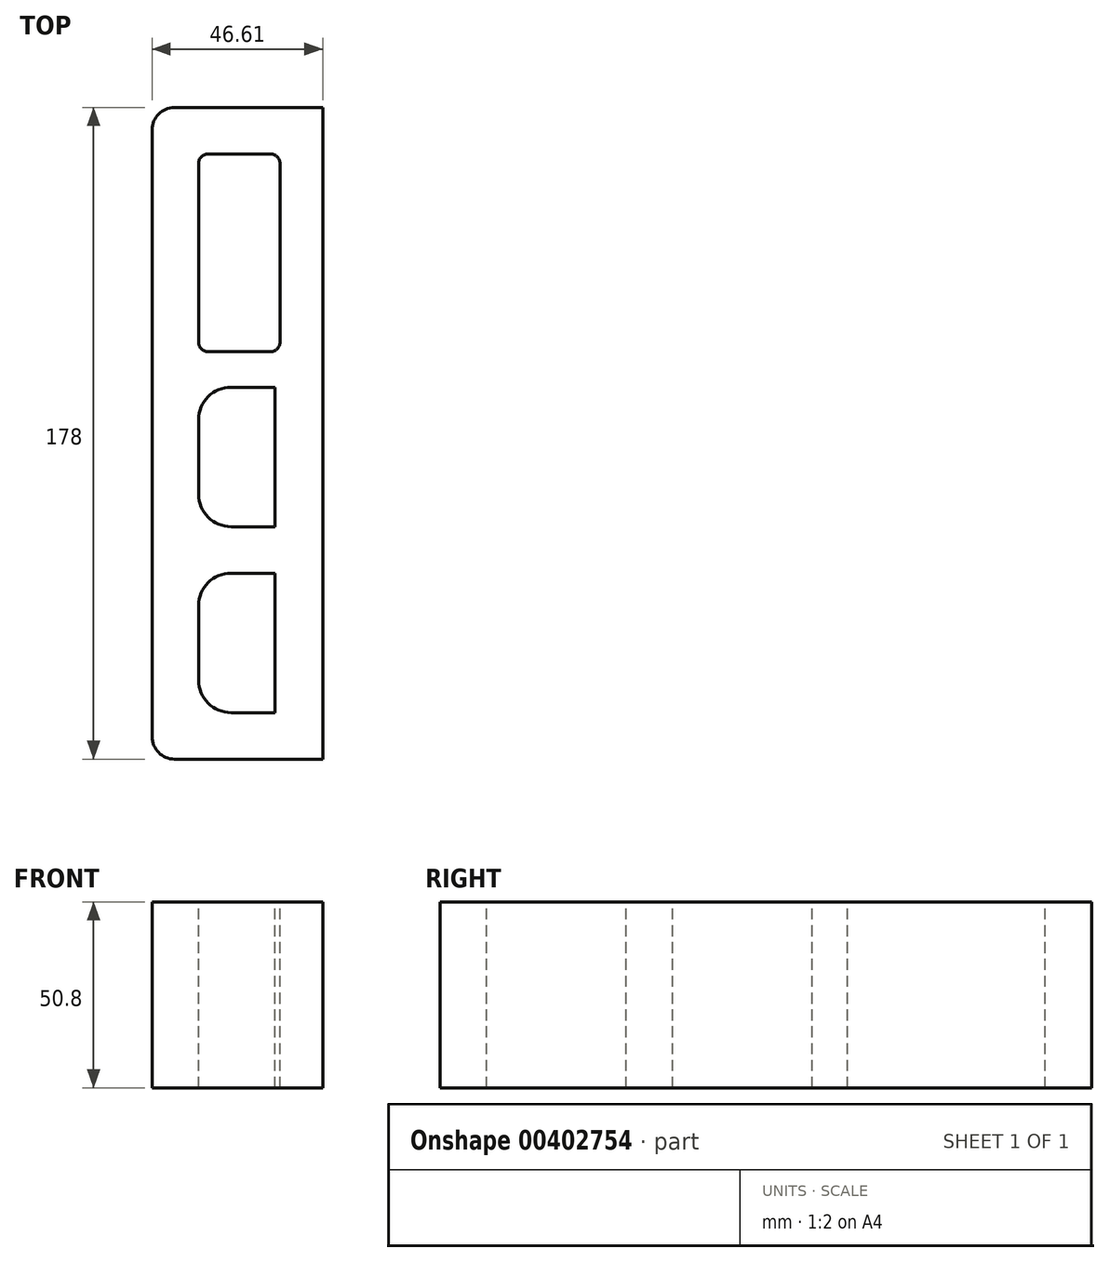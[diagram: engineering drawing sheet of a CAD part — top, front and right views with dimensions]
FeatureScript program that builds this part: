
annotation { "Feature Type Name" : "Feature", "Feature Type Description" : "" }
export const myFeature = defineFeature(function(context is Context, id is Id, definition is map)
    precondition{}
    {
        {
            var Q0;
            Q0=qCreatedBy(makeId("Top.planeOp"),FACE);
            var sketch = newSketch(context, id + "F0", { "sketchPlane" : qUnion([Q0])});
            skLineSegment(sketch, "E0", {"start": v(-117.43, 89) * mm, "end": v(117.43, -89) * mm, "construction": true});
            skLineSegment(sketch, "E1", {"start": v(117.43, 89) * mm, "end": v(0, 0) * mm, "construction": true});
            skArc(sketch, "E2", {"start": v(-70.48, 61.75) * mm, "mid": v(-79.05, 58.35) * mm, "end": v(-83.6, 50.33) * mm, "construction": true});
            skArc(sketch, "E3", {"start": v(-79.19, 70.45) * mm, "mid": v(-88.89, 80.1) * mm, "end": v(-98.64, 70.5) * mm, "construction": true});
            skArc(sketch, "E4", {"start": v(-98.68, -70.37) * mm, "mid": v(-88.97, -80.06) * mm, "end": v(-79.13, -70.5) * mm, "construction": true});
            skArc(sketch, "E5", {"start": v(-60.91, 9.68) * mm, "mid": v(-61.6, -0.56) * mm, "end": v(-60.92, -10.8) * mm});
            skLineSegment(sketch, "E6", {"start": v(-79.19, 70.45) * mm, "end": v(-70.48, 70.45) * mm, "construction": true});
            skLineSegment(sketch, "E7", {"start": v(-70.48, 70.45) * mm, "end": v(-70.48, 61.75) * mm, "construction": true});
            skLineSegment(sketch, "E8", {"start": v(-83.6, 50.33) * mm, "end": v(-83.6, 22.87) * mm, "construction": true});
            skLineSegment(sketch, "E9", {"start": v(-83.6, 22.87) * mm, "end": v(-77.26, 22.87) * mm, "construction": true});
            skLineSegment(sketch, "E10", {"start": v(-77.26, 22.87) * mm, "end": v(-77.26, -10.83) * mm, "construction": true});
            skLineSegment(sketch, "E11", {"start": v(-77.26, -10.83) * mm, "end": v(-70.83, -10.83) * mm, "construction": true});
            skLineSegment(sketch, "E12", {"start": v(-70.83, -10.83) * mm, "end": v(-70.83, -70.5) * mm, "construction": true});
            skLineSegment(sketch, "E13", {"start": v(-70.83, -70.5) * mm, "end": v(-79.13, -70.5) * mm, "construction": true});
            skLineSegment(sketch, "E14", {"start": v(-98.68, -70.37) * mm, "end": v(-105.43, -65.75) * mm, "construction": true});
            skLineSegment(sketch, "E15", {"start": v(-108.04, -64.7) * mm, "end": v(-108.04, -60.76) * mm, "construction": true});
            skLineSegment(sketch, "E16", {"start": v(-108.04, -60.76) * mm, "end": v(-106.9, -60.74) * mm, "construction": true});
            skLineSegment(sketch, "E17", {"start": v(-106.9, -60.74) * mm, "end": v(-106.9, 53.14) * mm, "construction": true});
            skLineSegment(sketch, "E18", {"start": v(-106.9, 53.14) * mm, "end": v(-108.07, 53.14) * mm, "construction": true});
            skLineSegment(sketch, "E19", {"start": v(-108.07, 53.14) * mm, "end": v(-108.07, 57.12) * mm, "construction": true});
            skLineSegment(sketch, "E20", {"start": v(-108.07, 57.12) * mm, "end": v(-106.9, 57.12) * mm, "construction": true});
            skLineSegment(sketch, "E21", {"start": v(-106.9, 57.12) * mm, "end": v(-107.04, 63.36) * mm, "construction": true});
            skLineSegment(sketch, "E22", {"start": v(-107.04, 63.36) * mm, "end": v(-98.64, 70.5) * mm, "construction": true});
            skArc(sketch, "E23", {"start": v(-9.49, 78.12) * mm, "mid": v(-18.8, 73.53) * mm, "end": v(-27.4, 67.74) * mm});
            skArc(sketch, "E24", {"start": v(75.52, 67.88) * mm, "mid": v(66.9, 73.6) * mm, "end": v(57.61, 78.19) * mm});
            skArc(sketch, "E25", {"start": v(108.1, -9.7) * mm, "mid": v(108.7, 0.59) * mm, "end": v(108.05, 10.87) * mm});
            skArc(sketch, "E26", {"start": v(56.9, -78.11) * mm, "mid": v(66.08, -73.32) * mm, "end": v(74.54, -67.34) * mm});
            skArc(sketch, "E27", {"start": v(-28.12, -67.82) * mm, "mid": v(-19.56, -73.56) * mm, "end": v(-10.29, -78.05) * mm});
            skArc(sketch, "E28", {"start": v(-28.4, 60.74) * mm, "mid": v(-45.75, 39.78) * mm, "end": v(-55.21, 14.26) * mm});
            skArc(sketch, "E29", {"start": v(50.94, 75.43) * mm, "mid": v(24.1, 80.05) * mm, "end": v(-2.74, 75.43) * mm});
            skArc(sketch, "E30", {"start": v(82.84, 54.94) * mm, "mid": v(79.78, 57.95) * mm, "end": v(76.52, 60.75) * mm});
            skArc(sketch, "E31", {"start": v(102.32, 15.8) * mm, "mid": v(101.51, 20.16) * mm, "end": v(100.4, 24.44) * mm});
            skArc(sketch, "E32", {"start": v(75.47, -60.27) * mm, "mid": v(92.86, -39.3) * mm, "end": v(102.35, -13.78) * mm});
            skArc(sketch, "E33", {"start": v(-3.58, -75.5) * mm, "mid": v(23.34, -80.12) * mm, "end": v(50.25, -75.43) * mm});
            skArc(sketch, "E34", {"start": v(-35.4, -54.87) * mm, "mid": v(-32.33, -57.87) * mm, "end": v(-29.07, -60.67) * mm});
            skArc(sketch, "E35", {"start": v(-55.22, -15.34) * mm, "mid": v(-54.43, -19.69) * mm, "end": v(-53.33, -23.97) * mm});
            skLineSegment(sketch, "E36", {"start": v(-55.22, -15.34) * mm, "end": v(-60.92, -10.8) * mm});
            skLineSegment(sketch, "E37", {"start": v(-60.91, 9.68) * mm, "end": v(-55.21, 14.26) * mm});
            skLineSegment(sketch, "E38", {"start": v(-28.4, 60.74) * mm, "end": v(-27.4, 67.74) * mm});
            skLineSegment(sketch, "E39", {"start": v(-9.49, 78.12) * mm, "end": v(-2.74, 75.43) * mm});
            skLineSegment(sketch, "E40", {"start": v(50.94, 75.43) * mm, "end": v(57.61, 78.19) * mm});
            skLineSegment(sketch, "E41", {"start": v(75.52, 67.88) * mm, "end": v(76.52, 60.75) * mm});
            skLineSegment(sketch, "E42", {"start": v(102.32, 15.8) * mm, "end": v(108.05, 10.87) * mm});
            skLineSegment(sketch, "E43", {"start": v(108.1, -9.7) * mm, "end": v(102.35, -13.78) * mm});
            skLineSegment(sketch, "E44", {"start": v(75.47, -60.27) * mm, "end": v(74.54, -67.34) * mm});
            skLineSegment(sketch, "E45", {"start": v(56.9, -78.11) * mm, "end": v(50.25, -75.43) * mm});
            skLineSegment(sketch, "E46", {"start": v(-10.29, -78.05) * mm, "end": v(-3.58, -75.5) * mm});
            skLineSegment(sketch, "E47", {"start": v(-28.12, -67.82) * mm, "end": v(-29.07, -60.67) * mm});
            skLineSegment(sketch, "E48", {"start": v(-117.43, 82.9) * mm, "end": v(-117.43, -82.9) * mm});
            skLineSegment(sketch, "E49", {"start": v(-111.33, -89) * mm, "end": v(111.33, -89) * mm});
            skLineSegment(sketch, "E50", {"start": v(117.43, -82.9) * mm, "end": v(117.43, 82.9) * mm});
            skLineSegment(sketch, "E51", {"start": v(111.33, 89) * mm, "end": v(-111.33, 89) * mm});
            skPoint(sketch, "E52.visualSharp", {"position": v(-117.43, 89) * mm});
            skArc(sketch, "E52.filletArc", {"start": v(-111.33, 89) * mm, "mid": v(-115.64, 87.21) * mm, "end": v(-117.43, 82.9) * mm});
            skPoint(sketch, "E53.visualSharp", {"position": v(117.43, 89) * mm});
            skArc(sketch, "E53.filletArc", {"start": v(117.43, 82.9) * mm, "mid": v(115.64, 87.21) * mm, "end": v(111.33, 89) * mm});
            skPoint(sketch, "E54.visualSharp", {"position": v(117.43, -89) * mm});
            skArc(sketch, "E54.filletArc", {"start": v(111.33, -89) * mm, "mid": v(115.64, -87.21) * mm, "end": v(117.43, -82.9) * mm});
            skPoint(sketch, "E55.visualSharp", {"position": v(-117.43, -89) * mm});
            skArc(sketch, "E55.filletArc", {"start": v(-117.43, -82.9) * mm, "mid": v(-115.64, -87.21) * mm, "end": v(-111.33, -89) * mm});
            skLineSegment(sketch, "E56", {"start": v(-108.04, -60.76) * mm, "end": v(-108.07, 53.14) * mm, "construction": true});
            skLineSegment(sketch, "E57", {"start": v(-107.04, 63.36) * mm, "end": v(-108.07, 57.12) * mm, "construction": true});
            skArc(sketch, "E58", {"start": v(-105.43, -65.75) * mm, "mid": v(-106.7, -65.12) * mm, "end": v(-108.04, -64.7) * mm, "construction": true});
            skArc(sketch, "E59", {"start": v(100.4, 24.44) * mm, "mid": v(104.45, 47.07) * mm, "end": v(82.84, 54.94) * mm});
            skArc(sketch, "E60", {"start": v(-53.33, -23.97) * mm, "mid": v(-59.81, -48.38) * mm, "end": v(-35.4, -54.87) * mm});
            skPoint(sketch, "E60.midSnap0", {"position": v(-35.4, -54.87) * mm});
            skPoint(sketch, "E60.midSnap1", {"position": v(-53.33, -23.97) * mm});
            skSolve(sketch);
        }
        {
            var Q0;
            Q0 = qSketchRegion(id + "F0", true);
            extrude(context, id + "F1", {"entities" : qUnion([Q0]), "depth" : 50.8 * mm, "offsetDistance" : 25.4 * mm});
        }
        {
            var Q0;
            Q0=makeQuery(id+"F1.opExtrude","CAP_FACE",FACE,{"disambiguationData":[OSD([sQuery(id+"F0.wireOp",EDGE,"E5"),sQuery(id+"F0.wireOp",EDGE,"E23"),sQuery(id+"F0.wireOp",EDGE,"E24"),sQuery(id+"F0.wireOp",EDGE,"E25"),sQuery(id+"F0.wireOp",EDGE,"E26"),sQuery(id+"F0.wireOp",EDGE,"E27"),sQuery(id+"F0.wireOp",EDGE,"E28"),sQuery(id+"F0.wireOp",EDGE,"E29"),sQuery(id+"F0.wireOp",EDGE,"E30"),sQuery(id+"F0.wireOp",EDGE,"E31"),sQuery(id+"F0.wireOp",EDGE,"E32"),sQuery(id+"F0.wireOp",EDGE,"E33"),sQuery(id+"F0.wireOp",EDGE,"E34"),sQuery(id+"F0.wireOp",EDGE,"E35"),sQuery(id+"F0.wireOp",EDGE,"E36"),sQuery(id+"F0.wireOp",EDGE,"E37"),sQuery(id+"F0.wireOp",EDGE,"E38"),sQuery(id+"F0.wireOp",EDGE,"E39"),sQuery(id+"F0.wireOp",EDGE,"E40"),sQuery(id+"F0.wireOp",EDGE,"E41"),sQuery(id+"F0.wireOp",EDGE,"E42"),sQuery(id+"F0.wireOp",EDGE,"E43"),sQuery(id+"F0.wireOp",EDGE,"E44"),sQuery(id+"F0.wireOp",EDGE,"E45"),sQuery(id+"F0.wireOp",EDGE,"E46"),sQuery(id+"F0.wireOp",EDGE,"E47"),sQuery(id+"F0.wireOp",EDGE,"E48"),sQuery(id+"F0.wireOp",EDGE,"E49"),sQuery(id+"F0.wireOp",EDGE,"E50"),sQuery(id+"F0.wireOp",EDGE,"E51"),sQuery(id+"F0.wireOp",EDGE,"E52.filletArc"),sQuery(id+"F0.wireOp",EDGE,"E53.filletArc"),sQuery(id+"F0.wireOp",EDGE,"E54.filletArc"),sQuery(id+"F0.wireOp",EDGE,"E55.filletArc"),sQuery(id+"F0.wireOp",EDGE,"E59"),sQuery(id+"F0.wireOp",EDGE,"E60")])],"isStart":false});
            var sketch = newSketch(context, id + "F2", { "sketchPlane" : qUnion([Q0])});
            skLineSegment(sketch, "E61.bottom", {"start": v(-104.73, -76.3) * mm, "end": v(-104.73, -38.2) * mm});
            skLineSegment(sketch, "E61.top", {"start": v(-83.9, -76.3) * mm, "end": v(-83.9, -38.2) * mm});
            skLineSegment(sketch, "E61.left", {"start": v(-104.73, -76.3) * mm, "end": v(-83.9, -76.3) * mm});
            skLineSegment(sketch, "E61.right", {"start": v(-104.73, -38.2) * mm, "end": v(-83.9, -38.2) * mm});
            skLineSegment(sketch, "E62", {"start": v(-62.2, -40.25) * mm, "end": v(-62.2, 42.66) * mm, "construction": true});
            skLineSegment(sketch, "E63", {"start": v(-62.2, 42.66) * mm, "end": v(-62.2, 89) * mm, "construction": true});
            skLineSegment(sketch, "E64", {"start": v(-62.2, -40.25) * mm, "end": v(-62.2, -89) * mm, "construction": true});
            skLineSegment(sketch, "E65", {"start": v(-62.2, -89) * mm, "end": v(-68.55, -89) * mm, "construction": true});
            skLineSegment(sketch, "E66", {"start": v(-68.55, -89) * mm, "end": v(-68.55, 89) * mm, "construction": true});
            skLineSegment(sketch, "E67", {"start": v(-70.82, -89) * mm, "end": v(-70.82, 89) * mm, "construction": true});
            skLineSegment(sketch, "E68.0.1.0", {"start": v(-104.73, -25.5) * mm, "end": v(-83.9, -25.5) * mm});
            skLineSegment(sketch, "E68.0.1.1", {"start": v(-104.73, -25.5) * mm, "end": v(-104.73, 12.6) * mm});
            skLineSegment(sketch, "E68.0.1.2", {"start": v(-83.9, -25.5) * mm, "end": v(-83.9, 12.6) * mm});
            skLineSegment(sketch, "E68.0.1.3", {"start": v(-104.73, 12.6) * mm, "end": v(-83.9, 12.6) * mm});
            skLineSegment(sketch, "E68.direction1", {"start": v(-104.73, -76.3) * mm, "end": v(-78.31, -76.3) * mm, "construction": true});
            skLineSegment(sketch, "E68.direction2", {"start": v(-104.73, -76.3) * mm, "end": v(-104.73, -25.5) * mm, "construction": true});
            skSolve(sketch);
        }
        {
            var Q0;
            Q0 = qSketchRegion(id + "F2", true);
            extrude(context, id + "F3", {"entities" : qUnion([Q0]), "operationType" : NewBodyOperationType.REMOVE, "oppositeDirection" : true, "depth" : 50.8 * mm, "offsetDistance" : 25.4 * mm});
        }
        {
            var Q0;
            Q0=makeQuery(id+"F1.opExtrude","CAP_FACE",FACE,{"disambiguationData":[OSD([sQuery(id+"F0.wireOp",EDGE,"E5"),sQuery(id+"F0.wireOp",EDGE,"E23"),sQuery(id+"F0.wireOp",EDGE,"E24"),sQuery(id+"F0.wireOp",EDGE,"E25"),sQuery(id+"F0.wireOp",EDGE,"E26"),sQuery(id+"F0.wireOp",EDGE,"E27"),sQuery(id+"F0.wireOp",EDGE,"E28"),sQuery(id+"F0.wireOp",EDGE,"E29"),sQuery(id+"F0.wireOp",EDGE,"E30"),sQuery(id+"F0.wireOp",EDGE,"E31"),sQuery(id+"F0.wireOp",EDGE,"E32"),sQuery(id+"F0.wireOp",EDGE,"E33"),sQuery(id+"F0.wireOp",EDGE,"E34"),sQuery(id+"F0.wireOp",EDGE,"E35"),sQuery(id+"F0.wireOp",EDGE,"E36"),sQuery(id+"F0.wireOp",EDGE,"E37"),sQuery(id+"F0.wireOp",EDGE,"E38"),sQuery(id+"F0.wireOp",EDGE,"E39"),sQuery(id+"F0.wireOp",EDGE,"E40"),sQuery(id+"F0.wireOp",EDGE,"E41"),sQuery(id+"F0.wireOp",EDGE,"E42"),sQuery(id+"F0.wireOp",EDGE,"E43"),sQuery(id+"F0.wireOp",EDGE,"E44"),sQuery(id+"F0.wireOp",EDGE,"E45"),sQuery(id+"F0.wireOp",EDGE,"E46"),sQuery(id+"F0.wireOp",EDGE,"E47"),sQuery(id+"F0.wireOp",EDGE,"E48"),sQuery(id+"F0.wireOp",EDGE,"E49"),sQuery(id+"F0.wireOp",EDGE,"E50"),sQuery(id+"F0.wireOp",EDGE,"E51"),sQuery(id+"F0.wireOp",EDGE,"E52.filletArc"),sQuery(id+"F0.wireOp",EDGE,"E53.filletArc"),sQuery(id+"F0.wireOp",EDGE,"E54.filletArc"),sQuery(id+"F0.wireOp",EDGE,"E55.filletArc"),sQuery(id+"F0.wireOp",EDGE,"E59"),sQuery(id+"F0.wireOp",EDGE,"E60")])],"isStart":false});
            var sketch = newSketch(context, id + "F4", { "sketchPlane" : qUnion([Q0])});
            skLineSegment(sketch, "E69.bottom", {"start": v(-104.73, 76.3) * mm, "end": v(-104.73, 22.32) * mm});
            skLineSegment(sketch, "E69.top", {"start": v(-82.5, 76.3) * mm, "end": v(-82.5, 22.32) * mm});
            skLineSegment(sketch, "E69.left", {"start": v(-104.73, 76.3) * mm, "end": v(-82.5, 76.3) * mm});
            skLineSegment(sketch, "E69.right", {"start": v(-104.73, 22.32) * mm, "end": v(-82.5, 22.32) * mm});
            skSolve(sketch);
        }
        {
            var Q0;
            Q0 = qSketchRegion(id + "F4", true);
            extrude(context, id + "F5", {"entities" : qUnion([Q0]), "operationType" : NewBodyOperationType.REMOVE, "oppositeDirection" : true, "depth" : 50.8 * mm, "offsetDistance" : 25.4 * mm});
        }
        {
            var Q0;
            Q0=makeQuery(id+"F3.boolean.opBoolean","COPY",EDGE,{"derivedFrom":makeQuery(id+"F3.opExtrude","SWEPT_EDGE",EDGE,{"disambiguationData":[OSD([sQuery(id+"F2.wireOp",EDGE,"E68.0.1.1"),sQuery(id+"F2.wireOp",EDGE,"E68.0.1.3")])]})});
            var Q1;
            Q1=makeQuery(id+"F3.boolean.opBoolean","COPY",EDGE,{"derivedFrom":makeQuery(id+"F3.opExtrude","SWEPT_EDGE",EDGE,{"disambiguationData":[OSD([sQuery(id+"F2.wireOp",EDGE,"E61.bottom"),sQuery(id+"F2.wireOp",EDGE,"E61.right")])]})});
            var Q2;
            Q2=makeQuery(id+"F3.boolean.opBoolean","COPY",EDGE,{"derivedFrom":makeQuery(id+"F3.opExtrude","SWEPT_EDGE",EDGE,{"disambiguationData":[OSD([sQuery(id+"F2.wireOp",EDGE,"E68.0.1.0"),sQuery(id+"F2.wireOp",EDGE,"E68.0.1.1")])]})});
            var Q3;
            Q3=makeQuery(id+"F3.boolean.opBoolean","COPY",EDGE,{"derivedFrom":makeQuery(id+"F3.opExtrude","SWEPT_EDGE",EDGE,{"disambiguationData":[OSD([sQuery(id+"F2.wireOp",EDGE,"E61.bottom"),sQuery(id+"F2.wireOp",EDGE,"E61.left")])]})});
            fillet(context, id + "F6", {"entities" : qUnion([Q0, Q1, Q2, Q3]), "tangentPropagation" : true, "radius" : 8.9 * mm, "defaultsChanged" : false, "vertexSettings" : [], "allowEdgeOverflow" : false});
        }
        {
            var Q0;
            Q0=makeQuery(id+"F5.boolean.opBoolean","COPY",EDGE,{"derivedFrom":makeQuery(id+"F5.opExtrude","SWEPT_EDGE",EDGE,{"disambiguationData":[OSD([sQuery(id+"F4.wireOp",EDGE,"E69.top"),sQuery(id+"F4.wireOp",EDGE,"E69.left")])]})});
            var Q1;
            Q1=makeQuery(id+"F5.boolean.opBoolean","COPY",EDGE,{"derivedFrom":makeQuery(id+"F5.opExtrude","SWEPT_EDGE",EDGE,{"disambiguationData":[OSD([sQuery(id+"F4.wireOp",EDGE,"E69.bottom"),sQuery(id+"F4.wireOp",EDGE,"E69.left")])]})});
            var Q2;
            Q2=makeQuery(id+"F5.boolean.opBoolean","COPY",EDGE,{"derivedFrom":makeQuery(id+"F5.opExtrude","SWEPT_EDGE",EDGE,{"disambiguationData":[OSD([sQuery(id+"F4.wireOp",EDGE,"E69.top"),sQuery(id+"F4.wireOp",EDGE,"E69.right")])]})});
            var Q3;
            Q3=makeQuery(id+"F5.boolean.opBoolean","COPY",EDGE,{"derivedFrom":makeQuery(id+"F5.opExtrude","SWEPT_EDGE",EDGE,{"disambiguationData":[OSD([sQuery(id+"F4.wireOp",EDGE,"E69.bottom"),sQuery(id+"F4.wireOp",EDGE,"E69.right")])]})});
            fillet(context, id + "F7", {"entities" : qUnion([Q0, Q1, Q2, Q3]), "tangentPropagation" : true, "radius" : 2.54 * mm, "defaultsChanged" : true, "vertexSettings" : [], "allowEdgeOverflow" : false});
        }
        {
            var Q0;
            Q0=makeQuery(id+"F1.opExtrude","CAP_FACE",FACE,{"disambiguationData":[OSD([sQuery(id+"F0.wireOp",EDGE,"E5"),sQuery(id+"F0.wireOp",EDGE,"E23"),sQuery(id+"F0.wireOp",EDGE,"E24"),sQuery(id+"F0.wireOp",EDGE,"E25"),sQuery(id+"F0.wireOp",EDGE,"E26"),sQuery(id+"F0.wireOp",EDGE,"E27"),sQuery(id+"F0.wireOp",EDGE,"E28"),sQuery(id+"F0.wireOp",EDGE,"E29"),sQuery(id+"F0.wireOp",EDGE,"E30"),sQuery(id+"F0.wireOp",EDGE,"E31"),sQuery(id+"F0.wireOp",EDGE,"E32"),sQuery(id+"F0.wireOp",EDGE,"E33"),sQuery(id+"F0.wireOp",EDGE,"E34"),sQuery(id+"F0.wireOp",EDGE,"E35"),sQuery(id+"F0.wireOp",EDGE,"E36"),sQuery(id+"F0.wireOp",EDGE,"E37"),sQuery(id+"F0.wireOp",EDGE,"E38"),sQuery(id+"F0.wireOp",EDGE,"E39"),sQuery(id+"F0.wireOp",EDGE,"E40"),sQuery(id+"F0.wireOp",EDGE,"E41"),sQuery(id+"F0.wireOp",EDGE,"E42"),sQuery(id+"F0.wireOp",EDGE,"E43"),sQuery(id+"F0.wireOp",EDGE,"E44"),sQuery(id+"F0.wireOp",EDGE,"E45"),sQuery(id+"F0.wireOp",EDGE,"E46"),sQuery(id+"F0.wireOp",EDGE,"E47"),sQuery(id+"F0.wireOp",EDGE,"E48"),sQuery(id+"F0.wireOp",EDGE,"E49"),sQuery(id+"F0.wireOp",EDGE,"E50"),sQuery(id+"F0.wireOp",EDGE,"E51"),sQuery(id+"F0.wireOp",EDGE,"E52.filletArc"),sQuery(id+"F0.wireOp",EDGE,"E53.filletArc"),sQuery(id+"F0.wireOp",EDGE,"E54.filletArc"),sQuery(id+"F0.wireOp",EDGE,"E55.filletArc"),sQuery(id+"F0.wireOp",EDGE,"E59"),sQuery(id+"F0.wireOp",EDGE,"E60")])],"isStart":false});
            var sketch = newSketch(context, id + "F8", { "sketchPlane" : qUnion([Q0])});
            skLineSegment(sketch, "E70.bottom", {"start": v(-70.82, 89) * mm, "end": v(205.99, 89) * mm});
            skLineSegment(sketch, "E70.top", {"start": v(-70.82, -129.87) * mm, "end": v(205.99, -129.87) * mm});
            skLineSegment(sketch, "E70.left", {"start": v(-70.82, 89) * mm, "end": v(-70.82, -129.87) * mm});
            skLineSegment(sketch, "E70.right", {"start": v(205.99, 89) * mm, "end": v(205.99, -129.87) * mm});
            skSolve(sketch);
        }
        {
            var Q0;
            Q0 = qSketchRegion(id + "F8", true);
            extrude(context, id + "F9", {"entities" : qUnion([Q0]), "operationType" : NewBodyOperationType.REMOVE, "oppositeDirection" : true, "depth" : 50.8 * mm, "offsetDistance" : 25.4 * mm});
        }
    });
